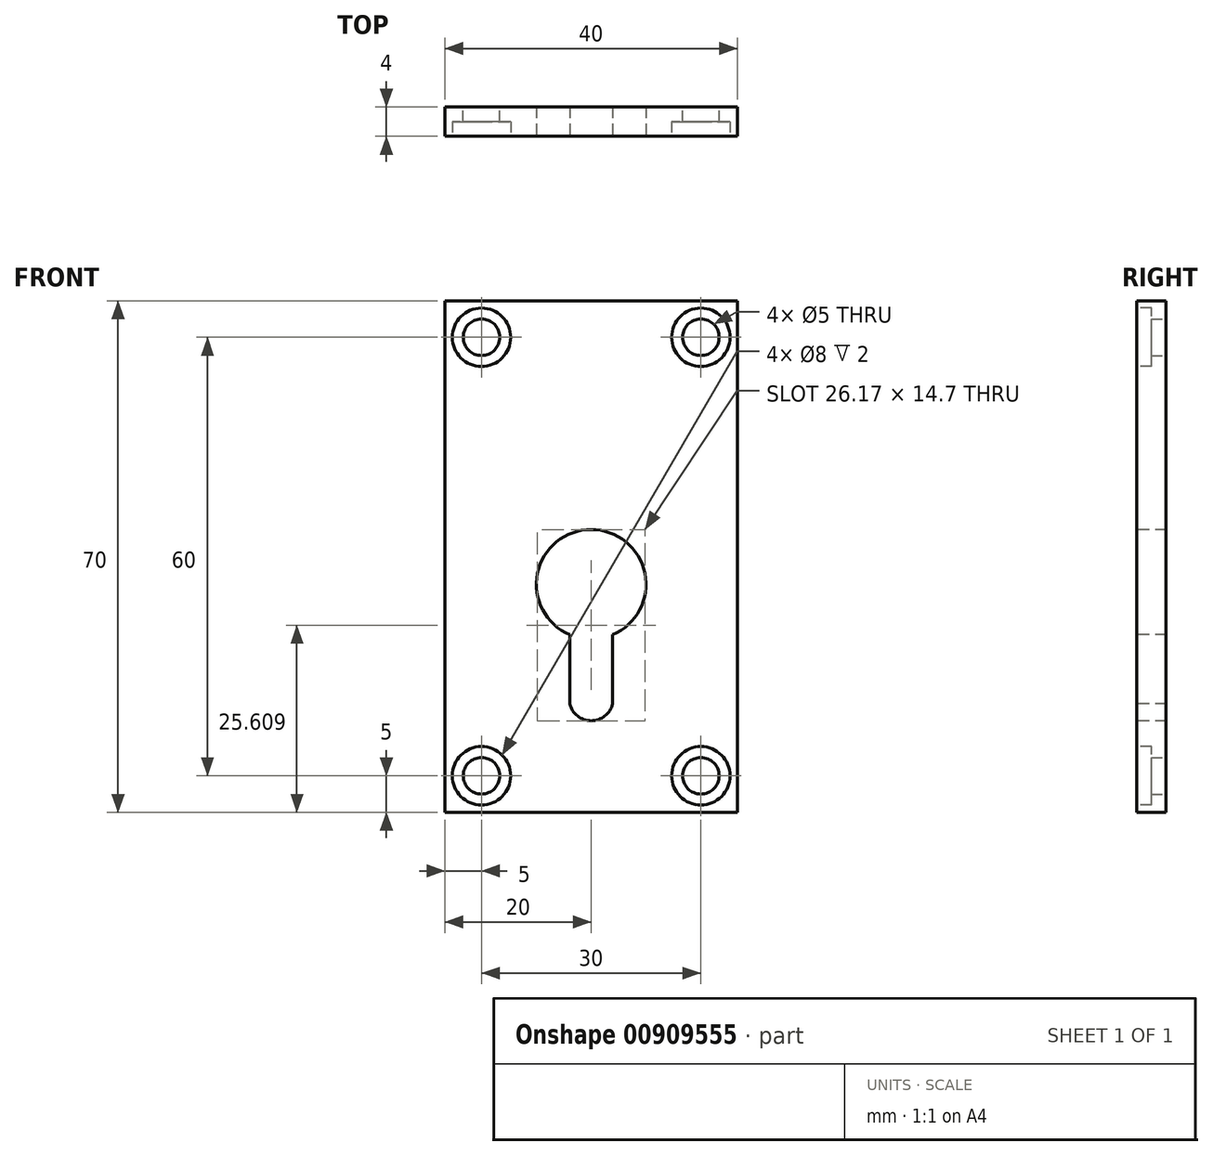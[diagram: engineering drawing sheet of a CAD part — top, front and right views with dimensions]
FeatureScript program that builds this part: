
annotation { "Feature Type Name" : "Feature", "Feature Type Description" : "" }
export const myFeature = defineFeature(function(context is Context, id is Id, definition is map)
    precondition{}
    {
        {
            var Q0;
            Q0=qCreatedBy(makeId("Front.planeOp"),FACE);
            var sketch = newSketch(context, id + "F0", { "sketchPlane" : qUnion([Q0])});
            skLineSegment(sketch, "E0.bottom", {"start": v(-20, 35) * mm, "end": v(20, 35) * mm});
            skLineSegment(sketch, "E0.top", {"start": v(-20, -35) * mm, "end": v(20, -35) * mm});
            skLineSegment(sketch, "E0.left", {"start": v(-20, 35) * mm, "end": v(-20, -35) * mm});
            skLineSegment(sketch, "E0.right", {"start": v(20, 35) * mm, "end": v(20, -35) * mm});
            skPoint(sketch, "E0.middle", {"position": v(0, 0) * mm});
            skCircle(sketch, "E1", {"center": v(-15, 30) * mm, "radius": 2.5 * mm});
            skCircle(sketch, "E2.0.1.0", {"center": v(-15, -30) * mm, "radius": 2.5 * mm});
            skCircle(sketch, "E2.1.0.0", {"center": v(15, 30) * mm, "radius": 2.5 * mm});
            skCircle(sketch, "E2.1.1.0", {"center": v(15, -30) * mm, "radius": 2.5 * mm});
            skLineSegment(sketch, "E2.direction1", {"start": v(-15, 30) * mm, "end": v(15, 30) * mm, "construction": true});
            skLineSegment(sketch, "E2.direction2", {"start": v(-15, 30) * mm, "end": v(-15, -30) * mm, "construction": true});
            skSolve(sketch);
        }
        {
            var Q0;
            Q0=makeQuery(id+"F0.imprint","IMPRINT",FACE,{"disambiguationData":[TD([[makeQuery(id+"F0.imprint","IMPRINT",EDGE,{"derivedFrom":sQuery(id+"F0.wireOp",EDGE,"E0.bottom")}),-1.0]])]});
            extrude(context, id + "F1", {"entities" : qUnion([Q0]), "depth" : 4 * mm, "offsetDistance" : 25 * mm});
        }
        {
            var Q0;
            Q0=makeQuery(id+"F1.opExtrude","CAP_FACE",FACE,{"disambiguationData":[OSD([sQuery(id+"F0.wireOp",EDGE,"E0.bottom"),sQuery(id+"F0.wireOp",EDGE,"E0.top"),sQuery(id+"F0.wireOp",EDGE,"E0.left"),sQuery(id+"F0.wireOp",EDGE,"E0.right"),sQuery(id+"F0.wireOp",EDGE,"E1"),sQuery(id+"F0.wireOp",EDGE,"E2.0.1.0"),sQuery(id+"F0.wireOp",EDGE,"E2.1.0.0"),sQuery(id+"F0.wireOp",EDGE,"E2.1.1.0")])],"isStart":false});
            var sketch = newSketch(context, id + "F2", { "sketchPlane" : qUnion([Q0])});
            skCircle(sketch, "E3", {"center": v(-15, 30) * mm, "radius": 4 * mm});
            skCircle(sketch, "E4", {"center": v(15, 30) * mm, "radius": 4 * mm});
            skCircle(sketch, "E5", {"center": v(15, -30) * mm, "radius": 4 * mm});
            skCircle(sketch, "E6", {"center": v(-15, -30) * mm, "radius": 4 * mm});
            skSolve(sketch);
        }
        {
            var Q0;
            Q0=makeQuery(id+"F2.imprint","IMPRINT",FACE,{"disambiguationData":[TD([[makeQuery(id+"F2.imprint","IMPRINT",EDGE,{"derivedFrom":makeQuery(id+"F1.opExtrude","CAP_EDGE",EDGE,{"disambiguationData":[OSD([sQuery(id+"F0.wireOp",EDGE,"E1")])],"isStart":false})}),1.0]])]});
            var Q1;
            Q1=makeQuery(id+"F2.imprint","IMPRINT",FACE,{"disambiguationData":[TD([[makeQuery(id+"F2.imprint","IMPRINT",EDGE,{"derivedFrom":makeQuery(id+"F1.opExtrude","CAP_EDGE",EDGE,{"disambiguationData":[OSD([sQuery(id+"F0.wireOp",EDGE,"E2.0.1.0")])],"isStart":false})}),1.0]])]});
            var Q2;
            Q2=makeQuery(id+"F2.imprint","IMPRINT",FACE,{"disambiguationData":[TD([[makeQuery(id+"F2.imprint","IMPRINT",EDGE,{"derivedFrom":makeQuery(id+"F1.opExtrude","CAP_EDGE",EDGE,{"disambiguationData":[OSD([sQuery(id+"F0.wireOp",EDGE,"E2.1.0.0")])],"isStart":false})}),1.0]])]});
            var Q3;
            Q3=makeQuery(id+"F2.imprint","IMPRINT",FACE,{"disambiguationData":[TD([[makeQuery(id+"F2.imprint","IMPRINT",EDGE,{"derivedFrom":makeQuery(id+"F1.opExtrude","CAP_EDGE",EDGE,{"disambiguationData":[OSD([sQuery(id+"F0.wireOp",EDGE,"E2.1.1.0")])],"isStart":false})}),1.0]])]});
            var Q4;
            Q4=makeQuery(id+"F2.imprint","IMPRINT",FACE,{"disambiguationData":[TD([[makeQuery(id+"F2.imprint","IMPRINT",EDGE,{"derivedFrom":sQuery(id+"F2.wireOp",EDGE,"E4")}),1.0]])]});
            var Q5;
            Q5=makeQuery(id+"F2.imprint","IMPRINT",FACE,{"disambiguationData":[TD([[makeQuery(id+"F2.imprint","IMPRINT",EDGE,{"derivedFrom":sQuery(id+"F2.wireOp",EDGE,"E5")}),1.0]])]});
            var Q6;
            Q6=makeQuery(id+"F2.imprint","IMPRINT",FACE,{"disambiguationData":[TD([[makeQuery(id+"F2.imprint","IMPRINT",EDGE,{"derivedFrom":sQuery(id+"F2.wireOp",EDGE,"E6")}),1.0]])]});
            var Q7;
            Q7=makeQuery(id+"F2.imprint","IMPRINT",FACE,{"disambiguationData":[TD([[makeQuery(id+"F2.imprint","IMPRINT",EDGE,{"derivedFrom":sQuery(id+"F2.wireOp",EDGE,"E3")}),1.0]])]});
            extrude(context, id + "F3", {"entities" : qUnion([Q0, Q1, Q2, Q3, Q4, Q5, Q6, Q7]), "operationType" : NewBodyOperationType.REMOVE, "oppositeDirection" : true, "depth" : 2 * mm, "offsetDistance" : 25 * mm});
        }
        {
            var Q0;
            Q0=makeQuery(id+"F1.opExtrude","CAP_FACE",FACE,{"disambiguationData":[OSD([sQuery(id+"F0.wireOp",EDGE,"E0.bottom"),sQuery(id+"F0.wireOp",EDGE,"E0.top"),sQuery(id+"F0.wireOp",EDGE,"E0.left"),sQuery(id+"F0.wireOp",EDGE,"E0.right"),sQuery(id+"F0.wireOp",EDGE,"E1"),sQuery(id+"F0.wireOp",EDGE,"E2.0.1.0"),sQuery(id+"F0.wireOp",EDGE,"E2.1.0.0"),sQuery(id+"F0.wireOp",EDGE,"E2.1.1.0")])],"isStart":false});
            var sketch = newSketch(context, id + "F4", { "sketchPlane" : qUnion([Q0])});
            skArc(sketch, "E7", {"start": v(2.92, -10.71) * mm, "mid": v(0, 3.7) * mm, "end": v(-2.92, -10.71) * mm});
            skArc(sketch, "E8", {"start": v(-2.92, -20.15) * mm, "mid": v(0, -22.47) * mm, "end": v(2.92, -20.15) * mm});
            skLineSegment(sketch, "E9", {"start": v(-2.92, -20.15) * mm, "end": v(-2.92, -10.71) * mm});
            skLineSegment(sketch, "E10", {"start": v(2.92, -20.15) * mm, "end": v(2.92, -10.71) * mm});
            skPoint(sketch, "E11.center.orphan", {"position": v(0, -15) * mm});
            skSolve(sketch);
        }
        {
            var Q0;
            Q0=makeQuery(id+"F4.imprint","IMPRINT",FACE,{"disambiguationData":[TD([[makeQuery(id+"F4.imprint","IMPRINT",EDGE,{"derivedFrom":sQuery(id+"F4.wireOp",EDGE,"E7")}),1.0]])]});
            extrude(context, id + "F5", {"entities" : qUnion([Q0]), "operationType" : NewBodyOperationType.REMOVE, "oppositeDirection" : true, "depth" : 25 * mm, "offsetDistance" : 25 * mm});
        }
    });
